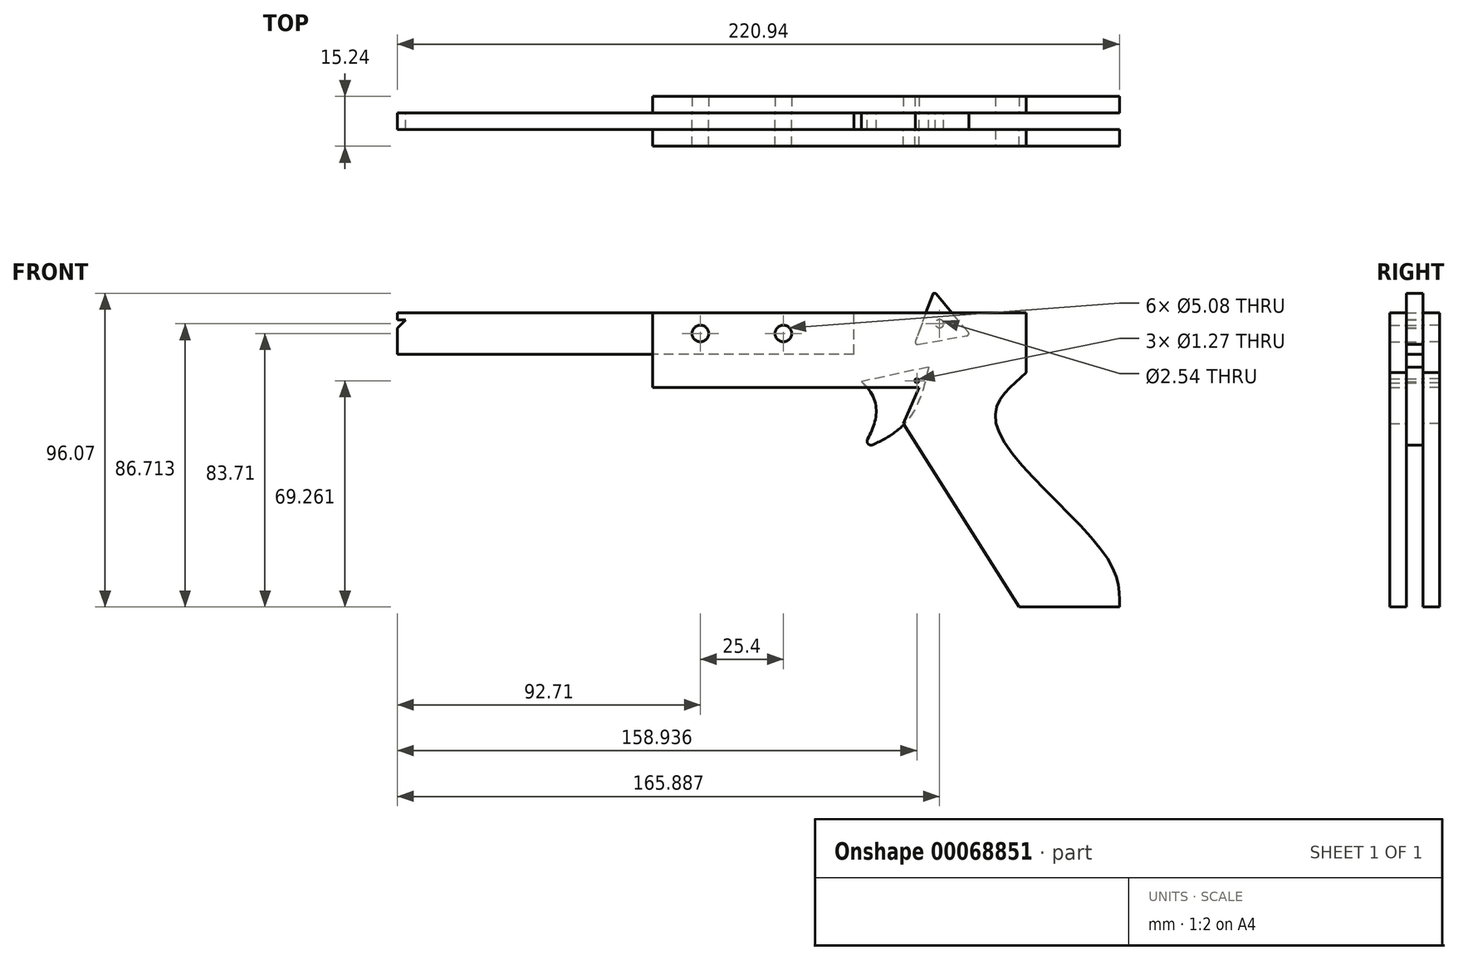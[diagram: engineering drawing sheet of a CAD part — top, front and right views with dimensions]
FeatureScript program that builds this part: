
annotation { "Feature Type Name" : "Feature", "Feature Type Description" : "" }
export const myFeature = defineFeature(function(context is Context, id is Id, definition is map)
    precondition{}
    {
        {
            var Q0;
            Q0=qCreatedBy(makeId("Front.planeOp"),FACE);
            var sketch = newSketch(context, id + "F0", { "sketchPlane" : qUnion([Q0])});
            skLineSegment(sketch, "E0.bottom", {"start": v(0, 0) * mm, "end": v(-139.7, 0) * mm});
            skLineSegment(sketch, "E0.top", {"start": v(0, 12.7) * mm, "end": v(-139.7, 12.7) * mm});
            skLineSegment(sketch, "E0.left", {"start": v(0, 0) * mm, "end": v(0, 12.7) * mm});
            skLineSegment(sketch, "E0.right", {"start": v(-139.7, 0) * mm, "end": v(-139.7, 12.7) * mm});
            skLineSegment(sketch, "E1", {"start": v(-139.7, 6.35) * mm, "end": v(0, 6.35) * mm, "construction": true});
            skCircle(sketch, "E2", {"center": v(-47, 6.35) * mm, "radius": 2.54 * mm});
            skCircle(sketch, "E3", {"center": v(-21.59, 6.35) * mm, "radius": 2.54 * mm});
            skLineSegment(sketch, "E4", {"start": v(-139.7, 8.01) * mm, "end": v(-137.17, 10.54) * mm});
            skLineSegment(sketch, "E5", {"start": v(-137.17, 10.54) * mm, "end": v(-139.7, 10.54) * mm});
            skSolve(sketch);
        }
        {
            var Q0;
            Q0=makeQuery(id+"F0.imprint","IMPRINT",FACE,{"disambiguationData":[TD([[makeQuery(id+"F0.imprint","IMPRINT",EDGE,{"derivedFrom":sQuery(id+"F0.wireOp",EDGE,"E0.bottom")}),-1.0]])]});
            extrude(context, id + "F1", {"entities" : qUnion([Q0]), "endBound" : BoundingType.SYMMETRIC, "depth" : 5.08 * mm});
        }
        {
            var Q0;
            Q0=makeQuery(id+"F1.opExtrude","CAP_FACE",FACE,{"disambiguationData":[OSD([sQuery(id+"F0.wireOp",EDGE,"E0.bottom"),sQuery(id+"F0.wireOp",EDGE,"E0.top"),sQuery(id+"F0.wireOp",EDGE,"E0.left"),sQuery(id+"F0.wireOp",EDGE,"E0.right"),sQuery(id+"F0.wireOp",EDGE,"E2"),sQuery(id+"F0.wireOp",EDGE,"E3"),sQuery(id+"F0.wireOp",EDGE,"E4"),sQuery(id+"F0.wireOp",EDGE,"E5")])],"isStart":false});
            var sketch = newSketch(context, id + "F2", { "sketchPlane" : qUnion([Q0])});
            skLineSegment(sketch, "E6.bottom", {"start": v(-61.63, 12.7) * mm, "end": v(52.67, 12.7) * mm});
            skLineSegment(sketch, "E6.top", {"start": v(-61.63, -10.16) * mm, "end": v(19.88, -10.16) * mm});
            skLineSegment(sketch, "E6.left", {"start": v(-61.63, 12.7) * mm, "end": v(-61.63, -10.16) * mm});
            skLineSegment(sketch, "E6.right", {"start": v(52.67, 12.7) * mm, "end": v(52.67, -10.16) * mm});
            skLineSegment(sketch, "E7", {"start": v(19.88, -10.16) * mm, "end": v(15.12, -21.2) * mm});
            skLineSegment(sketch, "E8", {"start": v(15.12, -21.2) * mm, "end": v(50.52, -77.36) * mm});
            skLineSegment(sketch, "E9", {"start": v(50.52, -77.36) * mm, "end": v(81.22, -77.36) * mm});
            skCircle(sketch, "E10.0", {"center": v(-47, 6.35) * mm, "radius": 2.54 * mm});
            skCircle(sketch, "E11.0", {"center": v(-21.59, 6.35) * mm, "radius": 2.54 * mm});
            skLineSegment(sketch, "E12", {"start": v(47.8, -10.16) * mm, "end": v(52.67, -5.63) * mm});
            skFitSpline(sketch, "E13", {"points": [v(47.8, -10.16) * mm, v(44, -23) * mm, v(77.1, -61.85) * mm, v(81.22, -77.36) * mm], "startDerivative": vector(-41.89, -38.95) * mm, "endDerivative": vector(-0.7, -50.34) * mm});
            skLineSegment(sketch, "E14.1.0", {"start": v(-15.05, 46.87) * mm, "end": v(-21.41, 48.82) * mm});
            skLineSegment(sketch, "E14.2.0", {"start": v(-33.02, -36.08) * mm, "end": v(-31.53, -42.56) * mm});
            skPoint(sketch, "E14.center", {"position": v(-0.1, 0.21) * mm});
            skLineSegment(sketch, "E15", {"start": v(44.35, -13.37) * mm, "end": v(52.67, -5.63) * mm, "construction": true});
            skLineSegment(sketch, "E16.trimOffspring", {"start": v(47.8, -10.16) * mm, "end": v(52.67, -10.16) * mm});
            skSolve(sketch);
        }
        {
            var Q0;
            {var subQ8=sQuery(id+"F2.wireOp",EDGE,"E6.top");Q0=makeQuery(id+"F2.imprint","IMPRINT",FACE,{"disambiguationData":[TD([[makeQuery(id+"F2.imprint","IMPRINT",EDGE,{"derivedFrom":subQ8}),1.0]])]});}
            var Q1;
            Q1=makeQuery(id+"F2.imprint","IMPRINT",FACE,{"disambiguationData":[TD([[makeQuery(id+"F2.imprint","IMPRINT",EDGE,{"derivedFrom":sQuery(id+"F2.wireOp",EDGE,"E10.0")}),-1.0]])]});
            extrude(context, id + "F3", {"entities" : qUnion([Q0, Q1]), "depth" : 5.08 * mm});
        }
        {
            var Q0;
            Q0=qCreatedBy(makeId("Front.planeOp"),FACE);
            var sketch = newSketch(context, id + "F4", { "sketchPlane" : qUnion([Q0])});
            skFitSpline(sketch, "E17", {"points": [v(22.81, -3.92) * mm, v(1.87, -29.55) * mm], "startDerivative": vector(-10.56, -52.91) * mm, "endDerivative": vector(-34.98, -15.93) * mm});
            skFitSpline(sketch, "E18", {"points": [v(2.28, -8.38) * mm, v(1.87, -29.55) * mm], "startDerivative": vector(24.2, -20.62) * mm, "endDerivative": vector(-12.31, -17.48) * mm});
            skLineSegment(sketch, "E19", {"start": v(22.81, -3.92) * mm, "end": v(2.28, -8.38) * mm});
            skCircle(sketch, "E20", {"center": v(19.24, -8.1) * mm, "radius": 0.64 * mm});
            skSolve(sketch);
        }
        {
            var Q0;
            Q0=makeQuery(id+"F4.imprint","IMPRINT",FACE,{"disambiguationData":[TD([[makeQuery(id+"F4.imprint","IMPRINT",EDGE,{"derivedFrom":sQuery(id+"F4.wireOp",EDGE,"E17")}),-1.0]])]});
            extrude(context, id + "F5", {"entities" : qUnion([Q0]), "endBound" : BoundingType.SYMMETRIC, "depth" : 5.08 * mm});
        }
        {
            var Q0;
            Q0=makeQuery(id+"F4.imprint","IMPRINT",FACE,{"disambiguationData":[TD([[makeQuery(id+"F4.imprint","IMPRINT",EDGE,{"derivedFrom":sQuery(id+"F4.wireOp",EDGE,"E20")}),1.0]])]});
            extrude(context, id + "F6", {"entities" : qUnion([Q0]), "operationType" : NewBodyOperationType.REMOVE, "endBound" : BoundingType.THROUGH_ALL, "depth" : 25.4 * mm});
        }
        {
            var Q0;
            Q0=makeQuery(id+"F3.opExtrude","SWEPT_BODY",BODY,{"disambiguationData":[OSD([sQuery(id+"F2.wireOp",EDGE,"E6.bottom"),sQuery(id+"F2.wireOp",EDGE,"E6.top"),sQuery(id+"F2.wireOp",EDGE,"E6.left"),sQuery(id+"F2.wireOp",EDGE,"E6.right"),sQuery(id+"F2.wireOp",EDGE,"E7"),sQuery(id+"F2.wireOp",EDGE,"E8"),sQuery(id+"F2.wireOp",EDGE,"E9"),sQuery(id+"F2.wireOp",EDGE,"E10.0"),sQuery(id+"F2.wireOp",EDGE,"E11.0"),sQuery(id+"F2.wireOp",EDGE,"E12"),sQuery(id+"F2.wireOp",EDGE,"E13")])]});
            var Q1;
            Q1=qCreatedBy(makeId("Front.planeOp"),FACE);
            mirror(context, id + "F7", {"entities" : qUnion([Q0]), "mirrorPlane" : qUnion([Q1])});
        }
        {
            var Q0;
            Q0=makeQuery(id+"F5.opExtrude","SWEPT_EDGE",EDGE,{"disambiguationData":[OSD([sQuery(id+"F4.wireOp",EDGE,"E17"),sQuery(id+"F4.wireOp",EDGE,"E18")])]});
            fillet(context, id + "F8", {"entities" : qUnion([Q0]), "radius" : 1.27 * mm, "tangentPropagation" : true, "allowEdgeOverflow" : false});
        }
        {
            var Q0;
            Q0=qCreatedBy(makeId("Front.planeOp"),FACE);
            var sketch = newSketch(context, id + "F9", { "sketchPlane" : qUnion([Q0])});
            skLineSegment(sketch, "E21", {"start": v(35.7, 5.88) * mm, "end": v(24.44, 19.32) * mm});
            skLineSegment(sketch, "E22", {"start": v(24.44, 19.32) * mm, "end": v(18.43, 2.85) * mm});
            skLineSegment(sketch, "E23", {"start": v(18.43, 2.85) * mm, "end": v(35.7, 5.88) * mm});
            skLineSegment(sketch, "E24", {"start": v(35.7, 5.88) * mm, "end": v(21.43, 11.09) * mm, "construction": true});
            skLineSegment(sketch, "E25", {"start": v(27.06, 4.37) * mm, "end": v(24.44, 19.32) * mm, "construction": true});
            skPoint(sketch, "E26", {"position": v(26.19, 9.35) * mm});
            skCircle(sketch, "E27", {"center": v(26.19, 9.35) * mm, "radius": 1.27 * mm});
            skSolve(sketch);
        }
        {
            var Q0;
            Q0=makeQuery(id+"F9.imprint","IMPRINT",FACE,{"disambiguationData":[TD([[makeQuery(id+"F9.imprint","IMPRINT",EDGE,{"derivedFrom":sQuery(id+"F9.wireOp",EDGE,"E21")}),1.0]])]});
            extrude(context, id + "F10", {"entities" : qUnion([Q0]), "endBound" : BoundingType.SYMMETRIC, "depth" : 5.08 * mm});
        }
        {
            var Q0;
            Q0=makeQuery(id+"F10.opExtrude","SWEPT_EDGE",EDGE,{"disambiguationData":[OSD([sQuery(id+"F9.wireOp",EDGE,"E21"),sQuery(id+"F9.wireOp",EDGE,"E22")])]});
            var Q1;
            Q1=makeQuery(id+"F10.opExtrude","SWEPT_EDGE",EDGE,{"disambiguationData":[OSD([sQuery(id+"F9.wireOp",EDGE,"E21"),sQuery(id+"F9.wireOp",EDGE,"E23")])]});
            var Q2;
            Q2=makeQuery(id+"F10.opExtrude","SWEPT_EDGE",EDGE,{"disambiguationData":[OSD([sQuery(id+"F9.wireOp",EDGE,"E22"),sQuery(id+"F9.wireOp",EDGE,"E23")])]});
            fillet(context, id + "F11", {"entities" : qUnion([Q0, Q1, Q2]), "radius" : 0.64 * mm, "tangentPropagation" : true, "allowEdgeOverflow" : false});
        }
        {
            var Q0;
            Q0=qCreatedBy(makeId("Front.planeOp"),FACE);
            var sketch = newSketch(context, id + "F12", { "sketchPlane" : qUnion([Q0])});
            skLineSegment(sketch, "E28", {"start": v(10.71, -10.16) * mm, "end": v(77.06, -10.16) * mm});
            skSolve(sketch);
        }
        {
            var Q0;
            Q0=sQuery(id+"F12.wireOp",EDGE,"E28");
            extrude(context, id + "F13", {"bodyType" : ToolBodyType.SURFACE, "surfaceEntities" : qUnion([Q0]), "depth" : 38.6 * mm, "hasSecondDirection" : true, "secondDirectionOppositeDirection" : true, "secondDirectionDepth" : 25.4 * mm});
        }
    });
